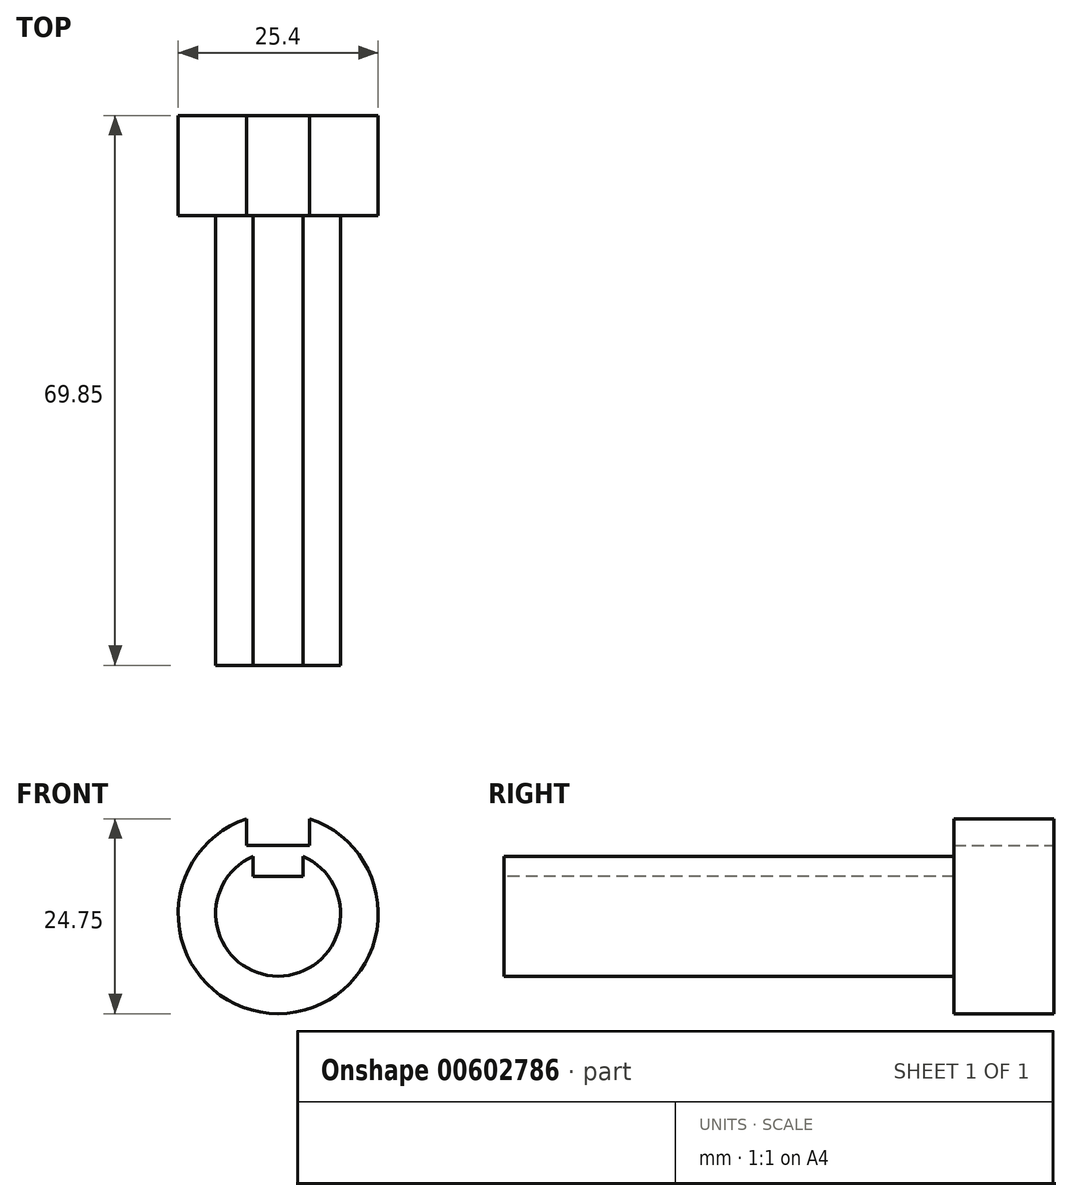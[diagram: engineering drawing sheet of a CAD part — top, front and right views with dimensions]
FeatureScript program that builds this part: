
annotation { "Feature Type Name" : "Feature", "Feature Type Description" : "" }
export const myFeature = defineFeature(function(context is Context, id is Id, definition is map)
    precondition{}
    {
        {
            var Q0;
            Q0=qCreatedBy(makeId("Front.planeOp"),FACE);
            var sketch = newSketch(context, id + "F0", { "sketchPlane" : qUnion([Q0])});
            skCircle(sketch, "E0", {"center": v(0, 0) * mm, "radius": 12.7 * mm});
            skSolve(sketch);
        }
        {
            var Q0;
            Q0 = qSketchRegion(id + "F0", true);
            extrude(context, id + "F1", {"entities" : qUnion([Q0]), "depth" : 12.7 * mm, "offsetDistance" : 25.4 * mm});
        }
        {
            var Q0;
            Q0=makeQuery(id+"F1.opExtrude","CAP_FACE",FACE,{"disambiguationData":[OSD([sQuery(id+"F0.wireOp",EDGE,"E0")])],"isStart":false});
            var sketch = newSketch(context, id + "F2", { "sketchPlane" : qUnion([Q0])});
            skCircle(sketch, "E1", {"center": v(0, 0) * mm, "radius": 7.94 * mm});
            skSolve(sketch);
        }
        {
            var Q0;
            Q0 = qSketchRegion(id + "F2", true);
            extrude(context, id + "F3", {"entities" : qUnion([Q0]), "operationType" : NewBodyOperationType.ADD, "depth" : 57.15 * mm, "offsetDistance" : 25.4 * mm});
        }
        {
            var Q0;
            Q0=makeQuery(id+"F1.opExtrude","CAP_FACE",FACE,{"disambiguationData":[OSD([sQuery(id+"F0.wireOp",EDGE,"E0")])],"isStart":true});
            var sketch = newSketch(context, id + "F4", { "sketchPlane" : qUnion([Q0])});
            skLineSegment(sketch, "E2.bottom", {"start": v(4, 8.7) * mm, "end": v(-4, 8.7) * mm});
            skLineSegment(sketch, "E2.top", {"start": v(4, 16.7) * mm, "end": v(-4, 16.7) * mm});
            skLineSegment(sketch, "E2.left", {"start": v(4, 8.7) * mm, "end": v(4, 16.7) * mm});
            skLineSegment(sketch, "E2.right", {"start": v(-4, 8.7) * mm, "end": v(-4, 16.7) * mm});
            skPoint(sketch, "E2.middle", {"position": v(0, 12.7) * mm});
            skSolve(sketch);
        }
        {
            var Q0;
            Q0 = qSketchRegion(id + "F4", true);
            extrude(context, id + "F5", {"entities" : qUnion([Q0]), "operationType" : NewBodyOperationType.REMOVE, "endBound" : BoundingType.THROUGH_ALL, "oppositeDirection" : true, "depth" : 25.4 * mm, "offsetDistance" : 25.4 * mm});
        }
        {
            var Q0;
            Q0=makeQuery(id+"F3.opExtrude","CAP_FACE",FACE,{"disambiguationData":[OSD([sQuery(id+"F2.wireOp",EDGE,"E1")])],"isStart":false});
            var sketch = newSketch(context, id + "F6", { "sketchPlane" : qUnion([Q0])});
            skLineSegment(sketch, "E3.bottom", {"start": v(3.17, 4.76) * mm, "end": v(-3.18, 4.76) * mm});
            skLineSegment(sketch, "E3.top", {"start": v(3.17, 11.11) * mm, "end": v(-3.18, 11.11) * mm});
            skLineSegment(sketch, "E3.left", {"start": v(3.17, 4.76) * mm, "end": v(3.17, 11.11) * mm});
            skLineSegment(sketch, "E3.right", {"start": v(-3.18, 4.76) * mm, "end": v(-3.18, 11.11) * mm});
            skPoint(sketch, "E3.middle", {"position": v(0, 7.94) * mm});
            skSolve(sketch);
        }
        {
            var Q0;
            Q0 = qSketchRegion(id + "F6", true);
            extrude(context, id + "F7", {"entities" : qUnion([Q0]), "operationType" : NewBodyOperationType.REMOVE, "oppositeDirection" : true, "depth" : 57.15 * mm, "offsetDistance" : 25.4 * mm});
        }
    });
